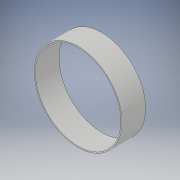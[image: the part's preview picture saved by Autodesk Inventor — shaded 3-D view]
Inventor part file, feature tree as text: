
AUTODESK INVENTOR PART (.ipt)
format: ipt  version: 2019 (Build 230136000, 136)  size: 104,960 bytes
history: native  units: mm
features: extrude x2, sketch x2
ambient origin geometry x8: Origin, YZ Plane, XZ Plane, XY Plane, X Axis, Y Axis, Z Axis, Center Point
bodies: Solid1 (feature_tree)
feature tree (4):
  extrude  "Extrusion1"  Depth=116.5mm TaperAngle=0.0deg
  extrude  "Extrusion2"  Depth=11.65mm TaperAngle=0.0deg
  sketch  "Sketch1"  dims[d0=430.0mm d1=116.5mm d2=0.0mm]
  sketch  "Sketch2"  dims[d3=420.0mm d4=11.65mm d5=0.0mm]
